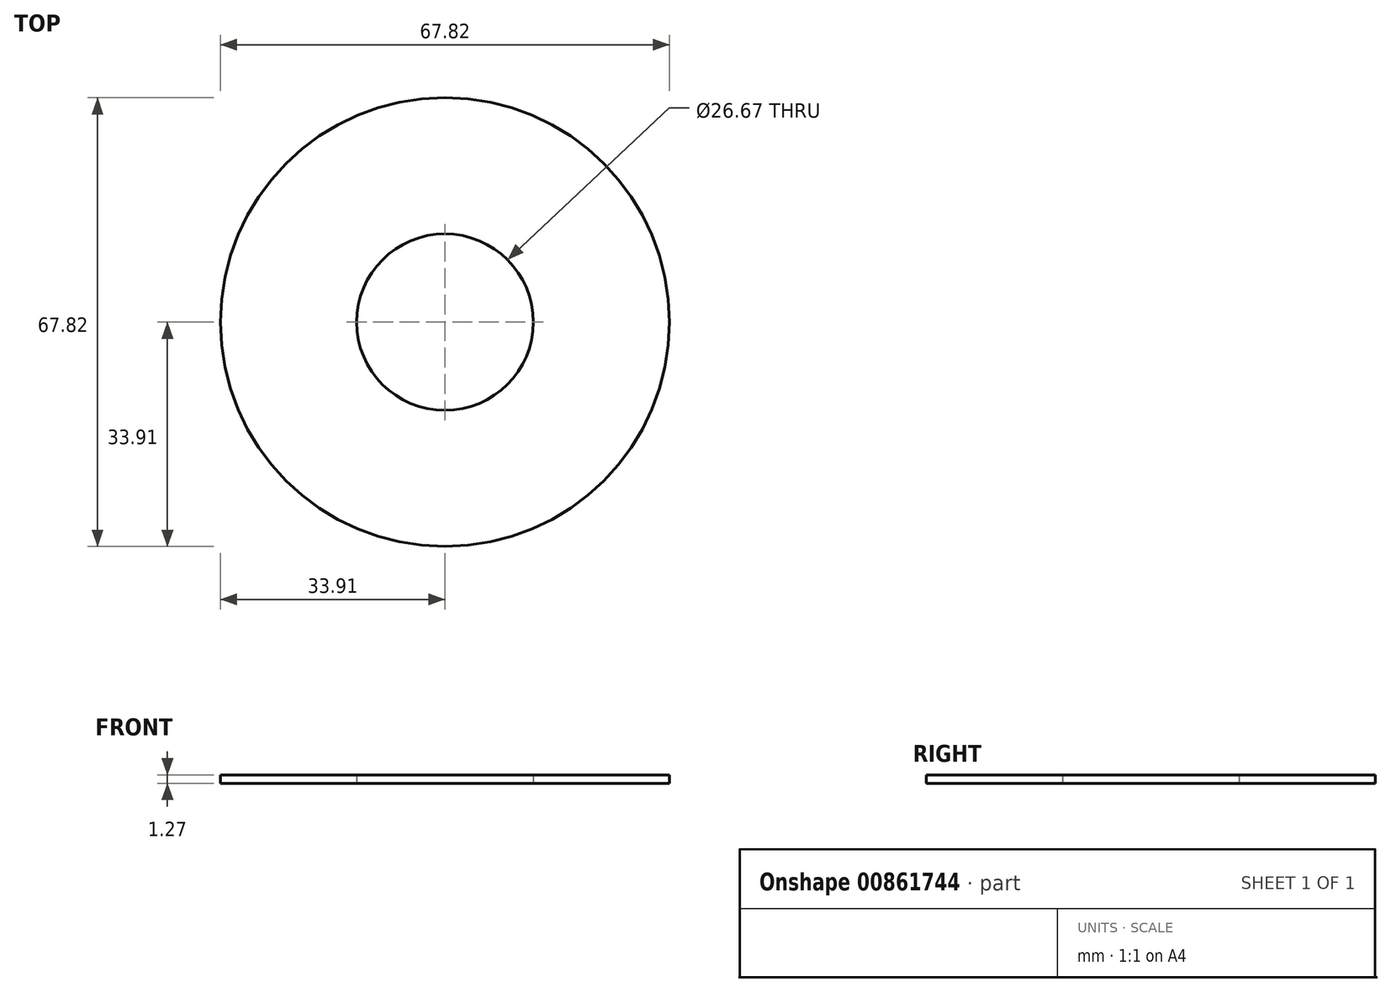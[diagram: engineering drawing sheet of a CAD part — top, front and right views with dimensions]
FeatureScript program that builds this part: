
annotation { "Feature Type Name" : "Feature", "Feature Type Description" : "" }
export const myFeature = defineFeature(function(context is Context, id is Id, definition is map)
    precondition{}
    {
        {
            var Q0;
            Q0=qCreatedBy(makeId("Top.planeOp"),FACE);
            var sketch = newSketch(context, id + "F0", { "sketchPlane" : qUnion([Q0])});
            skCircle(sketch, "E0", {"center": v(0, 0) * mm, "radius": 33.9 * mm});
            skCircle(sketch, "E1", {"center": v(0, 0) * mm, "radius": 13.34 * mm});
            skSolve(sketch);
        }
        {
            var Q0;
            Q0=makeQuery(id+"F0.imprint","IMPRINT",FACE,{"disambiguationData":[TD([[makeQuery(id+"F0.imprint","IMPRINT",EDGE,{"derivedFrom":sQuery(id+"F0.wireOp",EDGE,"E0")}),1.0]])]});
            extrude(context, id + "F1", {"entities" : qUnion([Q0]), "depth" : 1.27 * mm, "offsetDistance" : 25.4 * mm});
        }
    });
